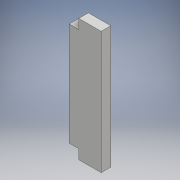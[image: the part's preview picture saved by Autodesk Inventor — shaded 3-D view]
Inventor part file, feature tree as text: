
AUTODESK INVENTOR PART (.ipt)
format: ipt  version: 2018 (Build 220112000, 112)  size: 104,448 bytes
history: native  units: mm
features: extrude x2, sketch x2, other x1
ambient origin geometry x8: Origin, YZ Plane, XZ Plane, XY Plane, X Axis, Y Axis, Z Axis, Center Point
bodies: Body1 (feature_tree)
feature tree (5):
  other  "Sólido1"
  extrude  "Extrusión1"  Depth=3.0mm TaperAngle=0.0deg
  extrude  "Extrusión3"  [1 undecoded]
  sketch  "Boceto1"  dims[d4=3.0mm d5=0.0mm d13=3.0mm d14=0.0mm]
  sketch  "Boceto3"
note: 1 required parameter value undecoded (feature->parameter linkage not recoverable at this tier; creation-order binding heuristic only, values carry confidence <= 0.55)
